# Revit family: Chair-Guest-Bernhardt-Sonar
name_source: partatom
category: Furniture
revit_build: Autodesk Revit Architecture 2013 (Build: 20130531_2115(x64)
units: mm (PartAtom-declared; Revit-internal decimal feet)

## types (5) — shared parameters
Depth = 1' - 9 1/2"
Description = Chair
Height = 2' - 7 1/2"
Manufacturer = Bernhardt Design
Metal Finish = Metal - Bernhardt Design - Polished Chrome
Product Documentation Link = http://www.bernhardtdesign.com
Product Name = Sonar
Product Page URL = http://www.bernhardtdesign.com
Seat Height = 1' - 6"
URL = http://www.bernhardtdesign.com
Width = 1' - 9"

## per-type parameters (varying)
| type | Back Finish | Seat Finish |
| 1126 | Wood - Bernhardt Design - Maple | Wood - Bernhardt Design - Maple |
| 1126U | Wood - Bernhardt Design - Maple | Fabric- Bernhardt Design - White Linen |
| 1127 | Wood - Bernhardt Design - Zebrawood | Wood - Bernhardt Design - Zebrawood |
| 1127U | Wood - Bernhardt Design - Zebrawood | Fabric- Bernhardt Design - White Linen |
| 1128 | Fabric- Bernhardt Design - White Linen | Fabric- Bernhardt Design - White Linen |

note: column(s) folded — value = type name in every type: Model

## geometry (parser evidence)
native form markers: Blend x8, Sweep x4
no freeform markers — native parametric forms only
